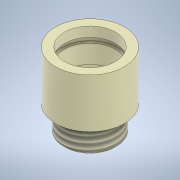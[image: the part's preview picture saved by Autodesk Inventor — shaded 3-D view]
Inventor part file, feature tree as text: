
AUTODESK INVENTOR PART (.ipt)
format: ipt  version: 2020.3 (Build 243373000, 373)  size: 160,256 bytes
history: native  units: mm
features: chamfer x2, revolve x1, fillet x1, thread x1, sketch x1
ambient origin geometry x8: Origin, YZ Plane, XZ Plane, XY Plane, X Axis, Y Axis, Z Axis, Center Point
bodies: Solid1 (feature_tree)
feature tree (6):
  revolve  "Revolution1"  [1 undecoded]
  fillet  "Fillet1"  Radius=4.0mm
  chamfer  "Chamfer1"  Distance=25.0mm
  chamfer  "Chamfer2"  Distance=4.5mm
  thread  "Thread1"  [1 undecoded]
  sketch  "Sketch1"  dims[d0=13.5mm d1=13.0mm d2=4.0mm d3=25.0mm d4=4.5mm d5=5.0mm d6=1.35mm d7=2.5mm d8=12.5mm d9=3.0mm d10=90.0deg d11=2.0mm d12=3.0mm d13=2.0mm d14=45.0deg d15=1.0mm d16=2.0mm d17=45.0deg d18=10.0mm d19=0.0mm]
note: 2 required parameter values undecoded (feature->parameter linkage not recoverable at this tier; creation-order binding heuristic only, values carry confidence <= 0.55)